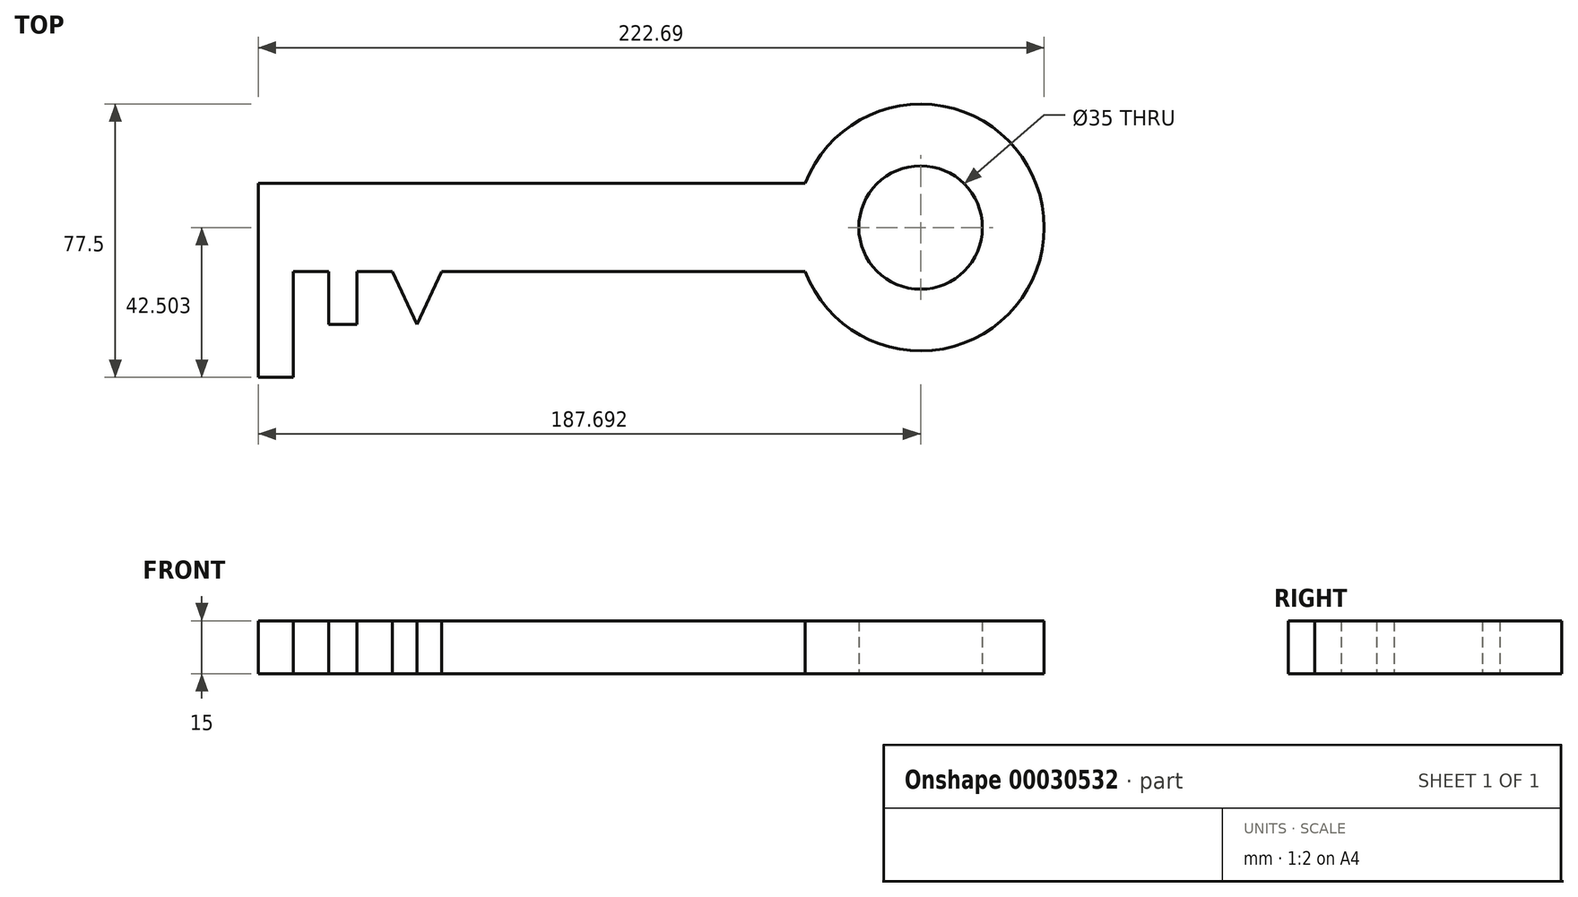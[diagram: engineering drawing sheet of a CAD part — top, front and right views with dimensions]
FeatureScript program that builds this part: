
annotation { "Feature Type Name" : "Feature", "Feature Type Description" : "" }
export const myFeature = defineFeature(function(context is Context, id is Id, definition is map)
    precondition{}
    {
        {
            var Q0;
            Q0=qCreatedBy(makeId("Top.planeOp"),FACE);
            var sketch = newSketch(context, id + "F0", { "sketchPlane" : qUnion([Q0])});
            skLineSegment(sketch, "E0.bottom", {"start": v(-88.18, 28) * mm, "end": v(-78.18, 28) * mm});
            skLineSegment(sketch, "E0.top", {"start": v(-98.18, 53) * mm, "end": v(56.82, 53) * mm});
            skLineSegment(sketch, "E0.left", {"start": v(-98.18, 28) * mm, "end": v(-98.18, 53) * mm});
            skLineSegment(sketch, "E1.top", {"start": v(-98.18, -2) * mm, "end": v(-88.18, -2) * mm});
            skLineSegment(sketch, "E1.left", {"start": v(-98.18, 28) * mm, "end": v(-98.18, -2) * mm});
            skLineSegment(sketch, "E1.right", {"start": v(-88.18, 28) * mm, "end": v(-88.18, -2) * mm});
            skLineSegment(sketch, "E2.top", {"start": v(-78.18, 13) * mm, "end": v(-70.18, 13) * mm});
            skLineSegment(sketch, "E2.left", {"start": v(-78.18, 28) * mm, "end": v(-78.18, 13) * mm});
            skLineSegment(sketch, "E2.right", {"start": v(-70.18, 28) * mm, "end": v(-70.18, 13) * mm});
            skLineSegment(sketch, "E3", {"start": v(-60.18, 28) * mm, "end": v(-53.18, 13) * mm});
            skLineSegment(sketch, "E4", {"start": v(-53.18, 13) * mm, "end": v(-46.18, 28) * mm});
            skArc(sketch, "E5", {"start": v(56.82, 28) * mm, "mid": v(124.51, 40.5) * mm, "end": v(56.82, 53) * mm});
            skCircle(sketch, "E6", {"center": v(89.51, 40.5) * mm, "radius": 17.5 * mm});
            skLineSegment(sketch, "E7", {"start": v(-98.18, 40.5) * mm, "end": v(89.51, 40.5) * mm, "construction": true});
            skLineSegment(sketch, "E8", {"start": v(-82.82, 40.5) * mm, "end": v(-98.18, 40.5) * mm, "construction": true});
            skLineSegment(sketch, "E9.trimOffspring", {"start": v(-46.18, 28) * mm, "end": v(56.82, 28) * mm});
            skLineSegment(sketch, "E10.trimOffspring", {"start": v(-70.18, 28) * mm, "end": v(-60.18, 28) * mm});
            skSolve(sketch);
        }
        {
            var Q0;
            Q0=makeQuery(id+"F0.imprint","IMPRINT",FACE,{"disambiguationData":[TD([[makeQuery(id+"F0.imprint","IMPRINT",EDGE,{"derivedFrom":sQuery(id+"F0.wireOp",EDGE,"E0.bottom")}),1.0]])]});
            extrude(context, id + "F1", {"entities" : qUnion([Q0]), "depth" : 15 * mm});
        }
    });
